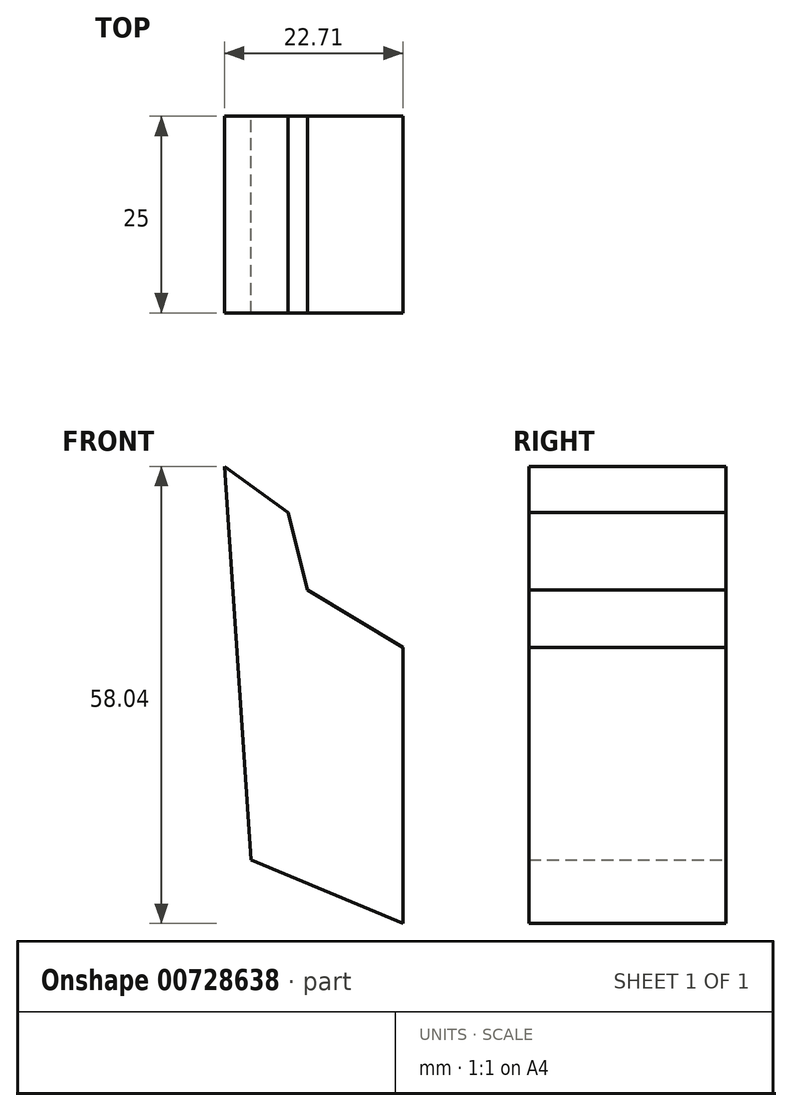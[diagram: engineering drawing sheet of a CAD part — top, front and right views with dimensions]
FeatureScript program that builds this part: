
annotation { "Feature Type Name" : "Feature", "Feature Type Description" : "" }
export const myFeature = defineFeature(function(context is Context, id is Id, definition is map)
    precondition{}
    {
        {
            var Q0;
            Q0=qCreatedBy(makeId("Front.planeOp"),FACE);
            var sketch = newSketch(context, id + "F0", { "sketchPlane" : qUnion([Q0])});
            skLineSegment(sketch, "E0", {"start": v(-46.57, 9.37) * mm, "end": v(-43.2, -40.6) * mm});
            skLineSegment(sketch, "E1", {"start": v(-43.2, -40.6) * mm, "end": v(-23.86, -48.67) * mm});
            skLineSegment(sketch, "E2", {"start": v(-23.86, -48.67) * mm, "end": v(-23.86, -13.64) * mm});
            skLineSegment(sketch, "E3", {"start": v(-23.86, -13.64) * mm, "end": v(-36.02, -6.31) * mm});
            skLineSegment(sketch, "E4", {"start": v(-36.02, -6.31) * mm, "end": v(-38.51, 3.5) * mm});
            skLineSegment(sketch, "E5", {"start": v(-38.51, 3.5) * mm, "end": v(-46.57, 9.37) * mm});
            skSolve(sketch);
        }
        {
            var Q0;
            Q0=makeQuery(id+"F0.imprint","IMPRINT",FACE,{"disambiguationData":[TD([[makeQuery(id+"F0.imprint","IMPRINT",EDGE,{"derivedFrom":sQuery(id+"F0.wireOp",EDGE,"E0")}),1.0]])]});
            extrude(context, id + "F1", {"entities" : qUnion([Q0]), "depth" : 25 * mm, "offsetDistance" : 25 * mm});
        }
    });
